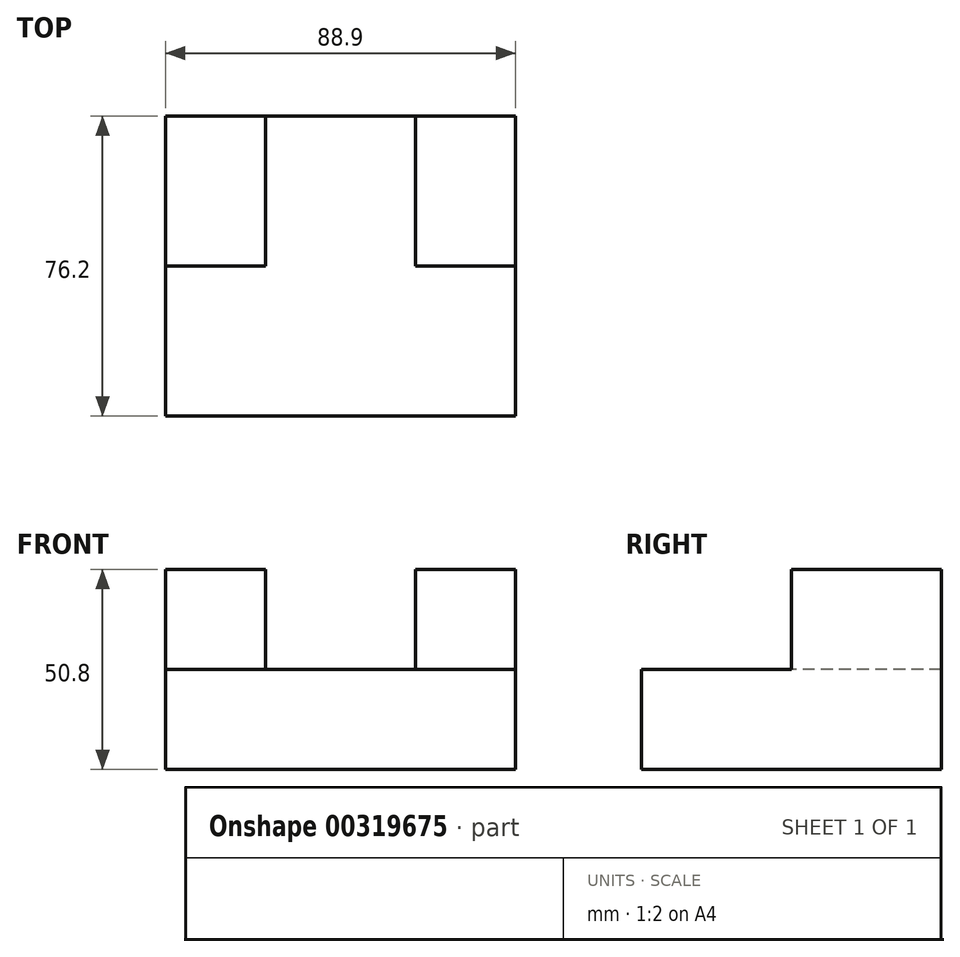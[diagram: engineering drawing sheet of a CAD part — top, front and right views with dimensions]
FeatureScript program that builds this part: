
annotation { "Feature Type Name" : "Feature", "Feature Type Description" : "" }
export const myFeature = defineFeature(function(context is Context, id is Id, definition is map)
    precondition{}
    {
        {
            var Q0;
            Q0=qCreatedBy(makeId("Right.planeOp"),FACE);
            var sketch = newSketch(context, id + "F0", { "sketchPlane" : qUnion([Q0])});
            skLineSegment(sketch, "E0", {"start": v(-46.84, -39.55) * mm, "end": v(29.36, -39.55) * mm});
            skLineSegment(sketch, "E1", {"start": v(29.36, -39.55) * mm, "end": v(29.36, -14.15) * mm});
            skLineSegment(sketch, "E2", {"start": v(29.36, -14.15) * mm, "end": v(-46.84, -14.15) * mm});
            skLineSegment(sketch, "E3", {"start": v(-46.84, -14.15) * mm, "end": v(-46.84, -39.55) * mm});
            skSolve(sketch);
        }
        {
            var Q0;
            Q0=makeQuery(id+"F0.imprint","IMPRINT",FACE,{"disambiguationData":[TD([[makeQuery(id+"F0.imprint","IMPRINT",EDGE,{"derivedFrom":sQuery(id+"F0.wireOp",EDGE,"E0")}),1.0]])]});
            extrude(context, id + "F1", {"entities" : qUnion([Q0]), "oppositeDirection" : true, "depth" : 88.9 * mm});
        }
        {
            var Q0;
            Q0=makeQuery(id+"F1.opExtrude","SWEPT_FACE",FACE,{"disambiguationData":[OSD([sQuery(id+"F0.wireOp",EDGE,"E2")])]});
            var sketch = newSketch(context, id + "F2", { "sketchPlane" : qUnion([Q0])});
            skLineSegment(sketch, "E4", {"start": v(0, 29.36) * mm, "end": v(0, -8.74) * mm});
            skLineSegment(sketch, "E5", {"start": v(0, -8.74) * mm, "end": v(-25.4, -8.74) * mm});
            skLineSegment(sketch, "E6", {"start": v(-25.4, -8.74) * mm, "end": v(-25.4, 29.36) * mm});
            skLineSegment(sketch, "E7", {"start": v(-25.4, 29.36) * mm, "end": v(0, 29.36) * mm});
            skLineSegment(sketch, "E8", {"start": v(-88.9, 29.36) * mm, "end": v(-63.5, 29.36) * mm});
            skLineSegment(sketch, "E9", {"start": v(-63.5, 29.36) * mm, "end": v(-63.5, -8.74) * mm});
            skLineSegment(sketch, "E10", {"start": v(-63.5, -8.74) * mm, "end": v(-88.9, -8.74) * mm});
            skLineSegment(sketch, "E11", {"start": v(-88.9, -8.74) * mm, "end": v(-88.9, 29.36) * mm});
            skSolve(sketch);
        }
        {
            var Q0;
            Q0=makeQuery(id+"F2.imprint","IMPRINT",FACE,{"disambiguationData":[TD([[makeQuery(id+"F2.imprint","IMPRINT",EDGE,{"derivedFrom":sQuery(id+"F2.wireOp",EDGE,"E4")}),-1.0]])]});
            var Q1;
            Q1=makeQuery(id+"F2.imprint","IMPRINT",FACE,{"disambiguationData":[TD([[makeQuery(id+"F2.imprint","IMPRINT",EDGE,{"derivedFrom":sQuery(id+"F2.wireOp",EDGE,"E8")}),-1.0]])]});
            extrude(context, id + "F3", {"entities" : qUnion([Q0, Q1]), "operationType" : NewBodyOperationType.ADD, "depth" : 25.4 * mm});
        }
    });
